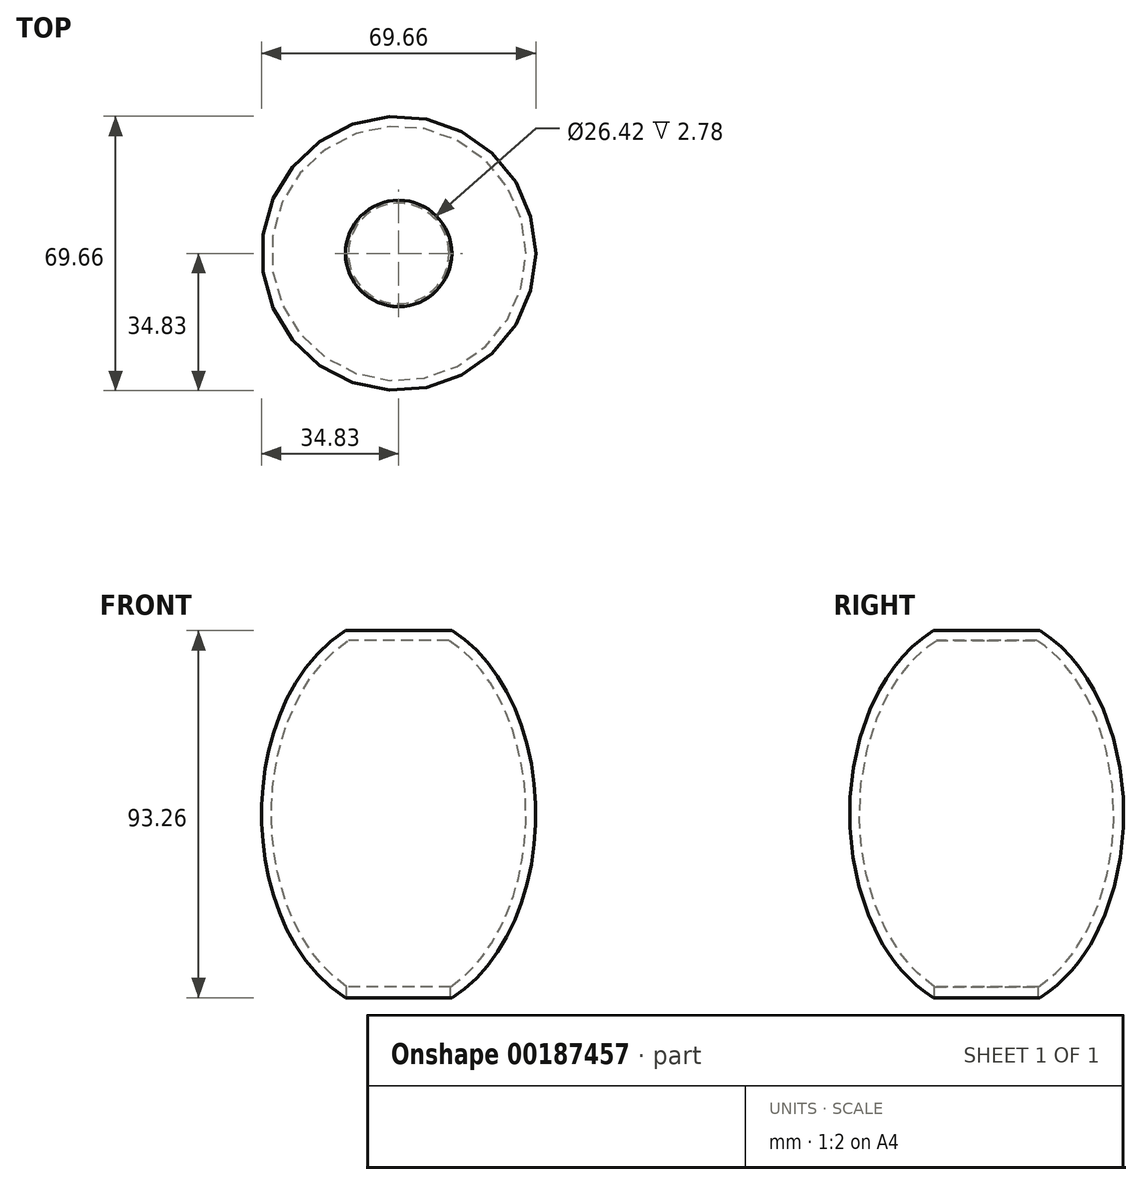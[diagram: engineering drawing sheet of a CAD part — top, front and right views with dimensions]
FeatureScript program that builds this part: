
annotation { "Feature Type Name" : "Feature", "Feature Type Description" : "" }
export const myFeature = defineFeature(function(context is Context, id is Id, definition is map)
    precondition{}
    {
        {
            var Q0;
            Q0=qCreatedBy(makeId("Front.planeOp"),FACE);
            var sketch = newSketch(context, id + "F5", { "sketchPlane" : qUnion([Q0])});
            skEllipticalArc(sketch, "E0", {});
            skLineSegment(sketch, "E1", {"start": v(13.5, 95.56) * mm, "end": v(13.5, -81.39) * mm, "construction": true});
            skLineSegment(sketch, "E2", {"start": v(0, 164) * mm, "end": v(0, -113.4) * mm, "construction": true});
            skLineSegment(sketch, "E3", {"start": v(13.5, 46.63) * mm, "end": v(0, 46.63) * mm});
            skLineSegment(sketch, "E4", {"start": v(13.5, -46.63) * mm, "end": v(0, -46.63) * mm});
            skLineSegment(sketch, "E5", {"start": v(0, 46.63) * mm, "end": v(0, -46.63) * mm});
            skLineSegment(sketch, "E6", {"start": v(117.42, 0) * mm, "end": v(-109.25, 0) * mm, "construction": true});
            const initialGuessFhwqy9MbNPFYpeewh_0  = {"E0": [0, 0, 0, -1, 0.05059319734573364, 0.03482891904376659, 0.39820496377943915, 2.7433876898103544]};
            skSetInitialGuess(sketch, initialGuessFhwqy9MbNPFYpeewh_0);
            skSolve(sketch);
        }
        {
            var Q0;
            Q0=makeQuery(id+"F5.imprint","IMPRINT",FACE,{"disambiguationData":[TD([[makeQuery(id+"F5.imprint","IMPRINT",EDGE,{"derivedFrom":sQuery(id+"F5.wireOp",EDGE,"E0")}),1.0]])]});
            var Q1;
            Q1=sQuery(id+"F5.wireOp",EDGE,"E2");
            revolve(context, id + "F0", {"entities" : qUnion([Q0]), "axis" : qUnion([Q1]), "revolveType" : RevolveType.FULL});
        }
        {
            var Q0;
            Q0=makeQuery(id+"F0.opRevolve","SWEPT_FACE",FACE,{"disambiguationData":[OSD([sQuery(id+"F5.wireOp",EDGE,"E0")])]});
            var Q1;
            Q1=makeQuery(id+"F0.opRevolve","SWEPT_BODY",BODY,{"disambiguationData":[OSD([sQuery(id+"F5.wireOp",EDGE,"E0"),sQuery(id+"F5.wireOp",EDGE,"E3"),sQuery(id+"F5.wireOp",EDGE,"E4"),sQuery(id+"F5.wireOp",EDGE,"E5")])]});
            shell(context, id + "F1", {"isHollow" : true, "entities" : qUnion([Q0]), "parts" : qUnion([Q1]), "thickness" : 2.5 * mm});
        }
        {
            var Q0;
            Q0=qCreatedBy(makeId("Top.planeOp"),FACE);
            var sketch = newSketch(context, id + "F2", { "sketchPlane" : qUnion([Q0])});
            skCircle(sketch, "E7", {"center": v(0, 0) * mm, "radius": 13.21 * mm});
            skSolve(sketch);
        }
        {
            var Q0;
            Q0 = qSketchRegion(id + "F2", true);
            extrude(context, id + "F3", {"entities" : qUnion([Q0]), "operationType" : NewBodyOperationType.REMOVE, "oppositeDirection" : true, "depth" : 74.17 * mm, "hasSecondDirection" : true, "secondDirectionOppositeDirection" : false, "secondDirectionDepth" : 25 * mm});
        }
    });
